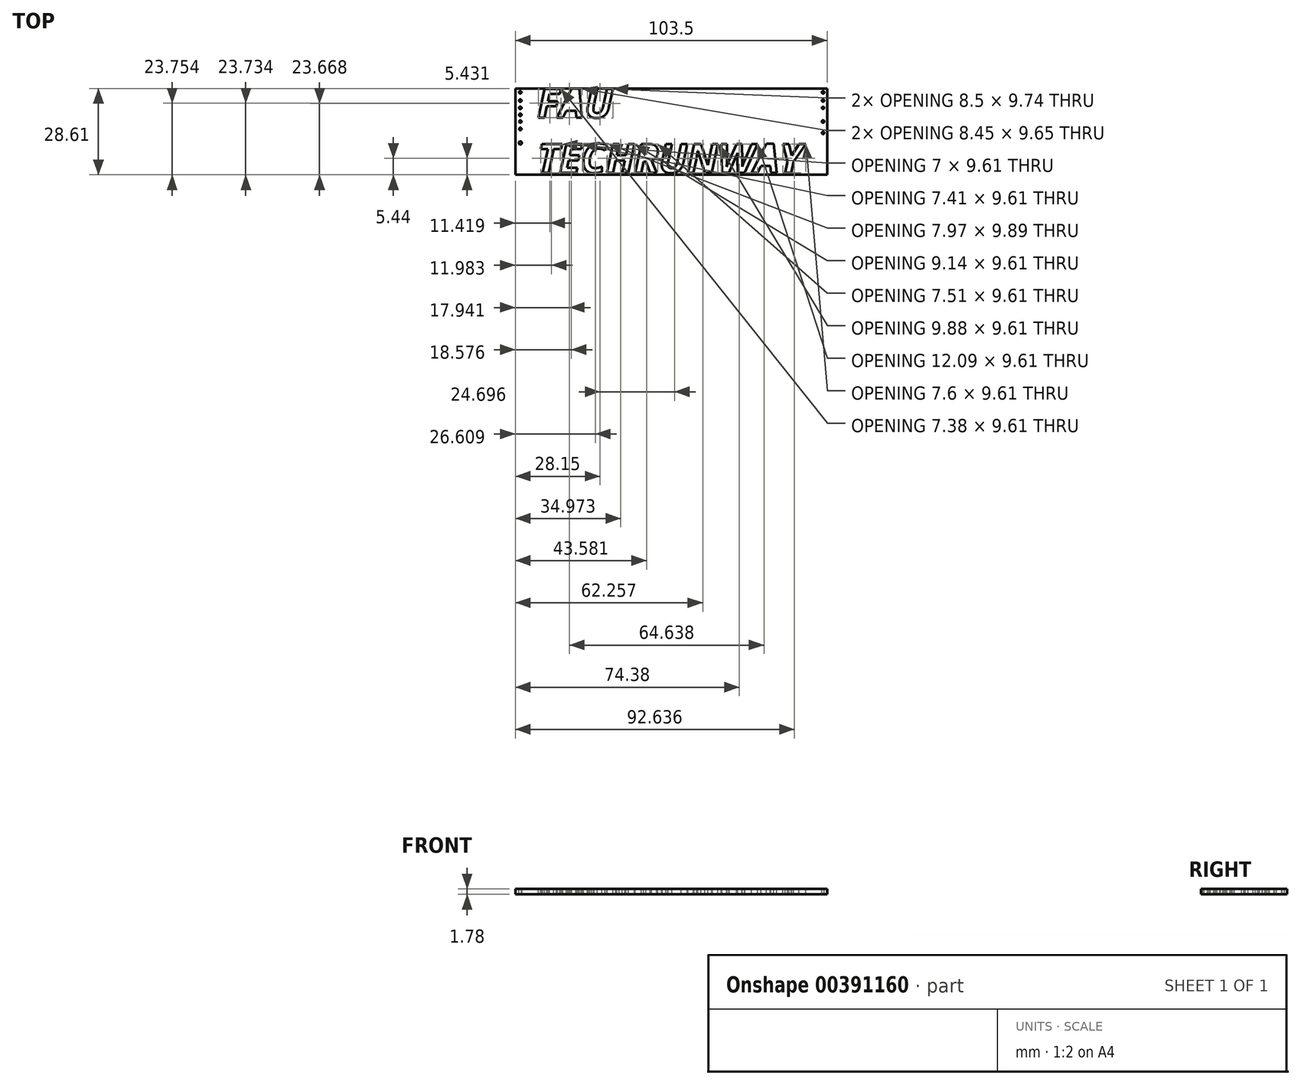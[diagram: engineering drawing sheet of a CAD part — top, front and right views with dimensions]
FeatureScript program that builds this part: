
annotation { "Feature Type Name" : "Feature", "Feature Type Description" : "" }
export const myFeature = defineFeature(function(context is Context, id is Id, definition is map)
    precondition{}
    {
        {
            var Q0;
            Q0=qCreatedBy(makeId("Top.planeOp"),FACE);
            var sketch = newSketch(context, id + "F0", { "sketchPlane" : qUnion([Q0])});
            skText(sketch, "E0", { "text": "FAU\nTECHRUNWAY", "fontName": "OpenSans-BoldItalic.ttf"});
            skLineSegment(sketch, "E1.bottom", {"start": v(-52.33, 25.35) * mm, "end": v(51.17, 25.35) * mm});
            skLineSegment(sketch, "E1.top", {"start": v(-52.33, -3.26) * mm, "end": v(51.17, -3.26) * mm});
            skLineSegment(sketch, "E1.left", {"start": v(-52.33, 25.35) * mm, "end": v(-52.33, -3.26) * mm});
            skLineSegment(sketch, "E1.right", {"start": v(51.17, 25.35) * mm, "end": v(51.17, -3.26) * mm});
            skCircle(sketch, "E2", {"center": v(-50.67, 24.1) * mm, "radius": 0.4 * mm});
            skCircle(sketch, "E3", {"center": v(-50.67, 21.36) * mm, "radius": 0.41 * mm});
            skCircle(sketch, "E4", {"center": v(-50.67, 18.95) * mm, "radius": 0.4 * mm});
            skCircle(sketch, "E5", {"center": v(-50.67, 16.62) * mm, "radius": 0.4 * mm});
            skCircle(sketch, "E6", {"center": v(-50.67, 14.41) * mm, "radius": 0.4 * mm});
            skCircle(sketch, "E7", {"center": v(-50.67, 11.94) * mm, "radius": 0.4 * mm});
            skCircle(sketch, "E8", {"center": v(-50.67, 7.3) * mm, "radius": 0.51 * mm});
            skCircle(sketch, "E9", {"center": v(49.84, 24.1) * mm, "radius": 0.4 * mm});
            skCircle(sketch, "E10", {"center": v(49.84, 21.36) * mm, "radius": 0.4 * mm});
            skCircle(sketch, "E11", {"center": v(49.84, 18.95) * mm, "radius": 0.35 * mm});
            skCircle(sketch, "E12", {"center": v(49.84, 14.41) * mm, "radius": 0.4 * mm});
            skCircle(sketch, "E13", {"center": v(49.84, 10.64) * mm, "radius": 0.4 * mm});
            const initialGuessF0  = {"E0": [-0.04495, 0.01567, 1, 0, 0.00969]};
            skSetInitialGuess(sketch, initialGuessF0);
            skSolve(sketch);
        }
        {
            var Q0;
            Q0 = qSketchRegion(id + "F0", true);
            extrude(context, id + "F1", {"entities" : qUnion([Q0]), "oppositeDirection" : true, "depth" : 1.78 * mm});
        }
    });
